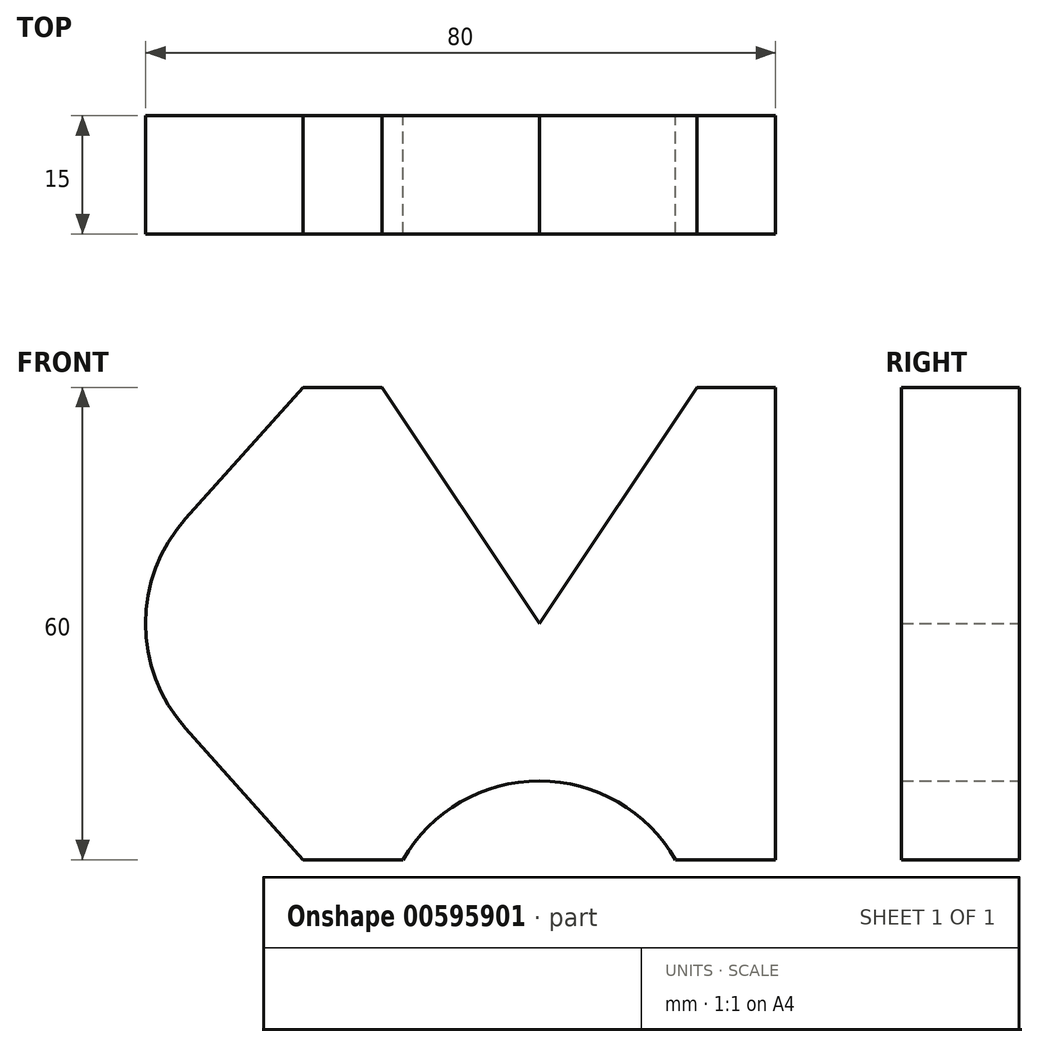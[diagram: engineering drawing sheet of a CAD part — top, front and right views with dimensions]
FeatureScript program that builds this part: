
annotation { "Feature Type Name" : "Feature", "Feature Type Description" : "" }
export const myFeature = defineFeature(function(context is Context, id is Id, definition is map)
    precondition{}
    {
        {
            var Q0;
            Q0=qCreatedBy(makeId("Front.planeOp"),FACE);
            var sketch = newSketch(context, id + "F0", { "sketchPlane" : qUnion([Q0])});
            skLineSegment(sketch, "E0", {"start": v(-30, 30) * mm, "end": v(-20, 30) * mm});
            skLineSegment(sketch, "E1", {"start": v(-20, 30) * mm, "end": v(0, 0) * mm});
            skLineSegment(sketch, "E2", {"start": v(0, 0) * mm, "end": v(20, 30) * mm});
            skLineSegment(sketch, "E3", {"start": v(20, 30) * mm, "end": v(30, 30) * mm});
            skLineSegment(sketch, "E4", {"start": v(30, 30) * mm, "end": v(30, -30) * mm});
            skLineSegment(sketch, "E5", {"start": v(30, -30) * mm, "end": v(17.32, -30) * mm});
            skArc(sketch, "E6", {"start": v(17.32, -30) * mm, "mid": v(0, -20) * mm, "end": v(-17.32, -30) * mm});
            skLineSegment(sketch, "E7", {"start": v(-17.32, -30) * mm, "end": v(-30, -30) * mm});
            skLineSegment(sketch, "E8", {"start": v(-30, -30) * mm, "end": v(-44.9, -13.33) * mm});
            skArc(sketch, "E9", {"start": v(-44.9, -13.33) * mm, "mid": v(-50, 0) * mm, "end": v(-44.9, 13.33) * mm});
            skLineSegment(sketch, "E10", {"start": v(-44.9, 13.33) * mm, "end": v(-30, 30) * mm});
            skLineSegment(sketch, "E11", {"start": v(-30, 30) * mm, "end": v(-30, -30) * mm, "construction": true});
            skSolve(sketch);
        }
        {
            var Q0;
            Q0=makeQuery(id+"F0.imprint","IMPRINT",FACE,{"disambiguationData":[TD([[makeQuery(id+"F0.imprint","IMPRINT",EDGE,{"derivedFrom":sQuery(id+"F0.wireOp",EDGE,"E0")}),-1.0]])]});
            extrude(context, id + "F1", {"entities" : qUnion([Q0]), "depth" : 15 * mm, "offsetDistance" : 25 * mm});
        }
    });
